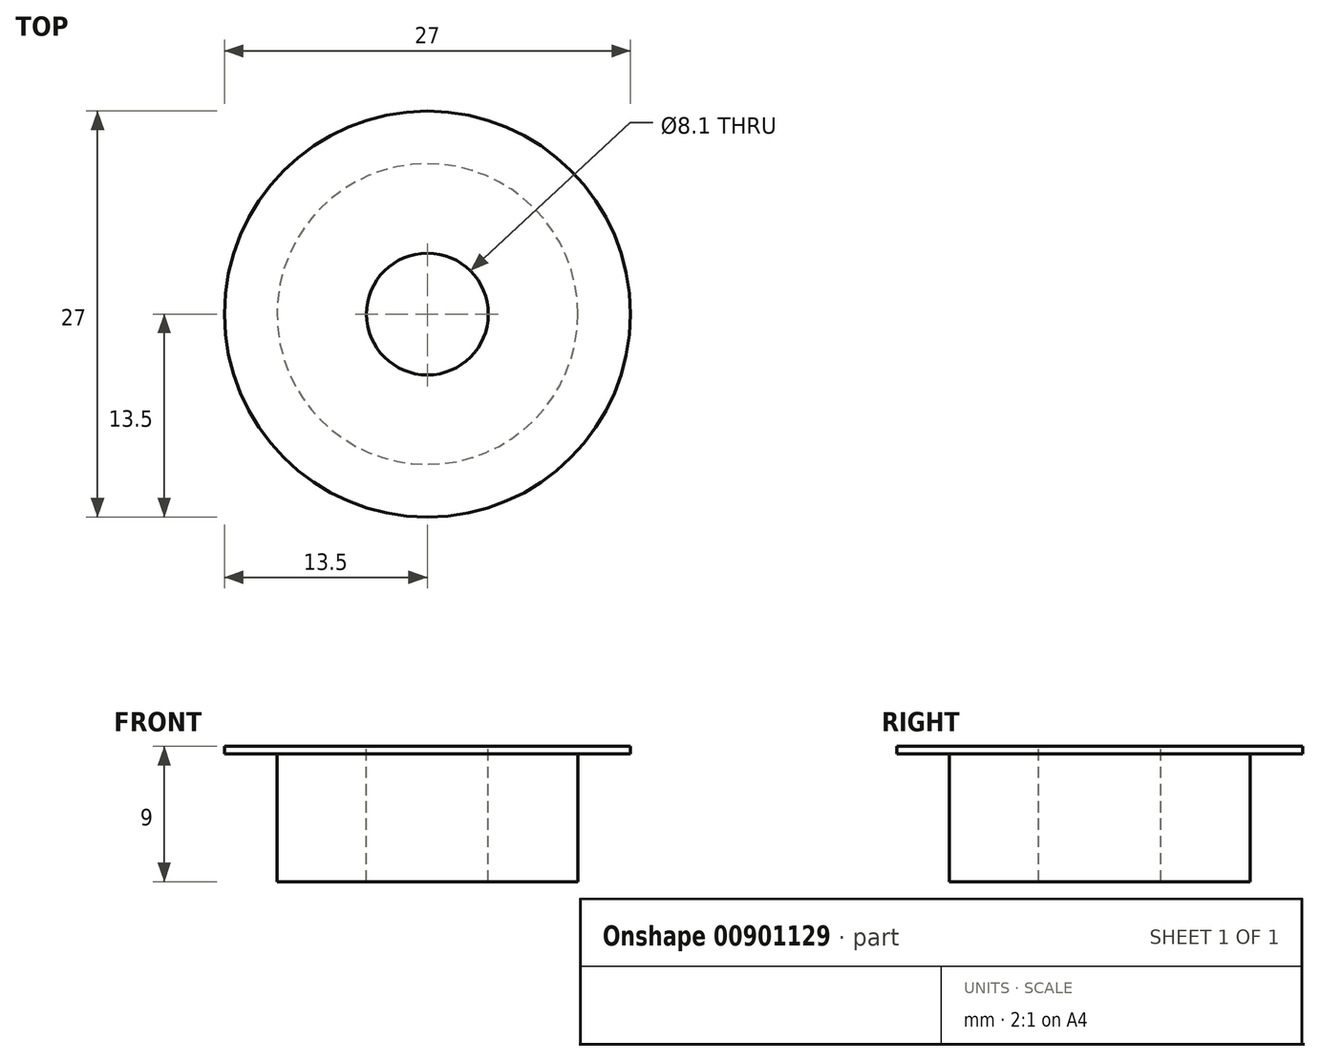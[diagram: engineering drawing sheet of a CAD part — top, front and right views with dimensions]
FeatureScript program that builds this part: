
annotation { "Feature Type Name" : "Feature", "Feature Type Description" : "" }
export const myFeature = defineFeature(function(context is Context, id is Id, definition is map)
    precondition{}
    {
        {
            var Q0;
            Q0=qCreatedBy(makeId("Top.planeOp"),FACE);
            var sketch = newSketch(context, id + "F0", { "sketchPlane" : qUnion([Q0])});
            skCircle(sketch, "E0", {"center": v(0, 0) * mm, "radius": 10 * mm});
            skSolve(sketch);
        }
        {
            var Q0;
            Q0=makeQuery(id+"F0.imprint","IMPRINT",FACE,{"disambiguationData":[TD([[makeQuery(id+"F0.imprint","IMPRINT",EDGE,{"derivedFrom":sQuery(id+"F0.wireOp",EDGE,"E0")}),1.0]])]});
            extrude(context, id + "F1", {"entities" : qUnion([Q0]), "depth" : (18 / 2 - 0.5) * mm, "offsetDistance" : 25 * mm});
        }
        {
            var Q0;
            Q0=makeQuery(id+"F1.opExtrude","CAP_FACE",FACE,{"disambiguationData":[OSD([sQuery(id+"F0.wireOp",EDGE,"E0")])],"isStart":false});
            var sketch = newSketch(context, id + "F2", { "sketchPlane" : qUnion([Q0])});
            skCircle(sketch, "E1", {"center": v(0, 0) * mm, "radius": 13.5 * mm});
            skSolve(sketch);
        }
        {
            var Q0;
            Q0=makeQuery(id+"F2.imprint","IMPRINT",FACE,{"disambiguationData":[TD([[makeQuery(id+"F2.imprint","IMPRINT",EDGE,{"derivedFrom":makeQuery(id+"F1.opExtrude","CAP_EDGE",EDGE,{"disambiguationData":[OSD([sQuery(id+"F0.wireOp",EDGE,"E0")])],"isStart":false})}),1.0]])]});
            var Q1;
            Q1=makeQuery(id+"F2.imprint","IMPRINT",FACE,{"disambiguationData":[TD([[makeQuery(id+"F2.imprint","IMPRINT",EDGE,{"derivedFrom":sQuery(id+"F2.wireOp",EDGE,"E1")}),1.0]])]});
            var Q2;
            Q2 = qSketchRegion(id + "F2", true);
            extrude(context, id + "F3", {"entities" : qUnion([Q0, Q1, Q2]), "operationType" : NewBodyOperationType.ADD, "depth" : 0.5 * mm, "offsetDistance" : 25 * mm});
        }
        {
            var Q0;
            Q0=makeQuery(id+"F3.opExtrude","CAP_FACE",FACE,{"disambiguationData":[OSD([sQuery(id+"F2.wireOp",EDGE,"E1")])],"isStart":false});
            var sketch = newSketch(context, id + "F4", { "sketchPlane" : qUnion([Q0])});
            skCircle(sketch, "E2", {"center": v(0, 0) * mm, "radius": 4.05 * mm});
            skSolve(sketch);
        }
        {
            var Q0;
            Q0 = qSketchRegion(id + "F4", true);
            extrude(context, id + "F5", {"entities" : qUnion([Q0]), "operationType" : NewBodyOperationType.REMOVE, "endBound" : BoundingType.THROUGH_ALL, "oppositeDirection" : true, "depth" : 25 * mm, "offsetDistance" : 25 * mm});
        }
    });
